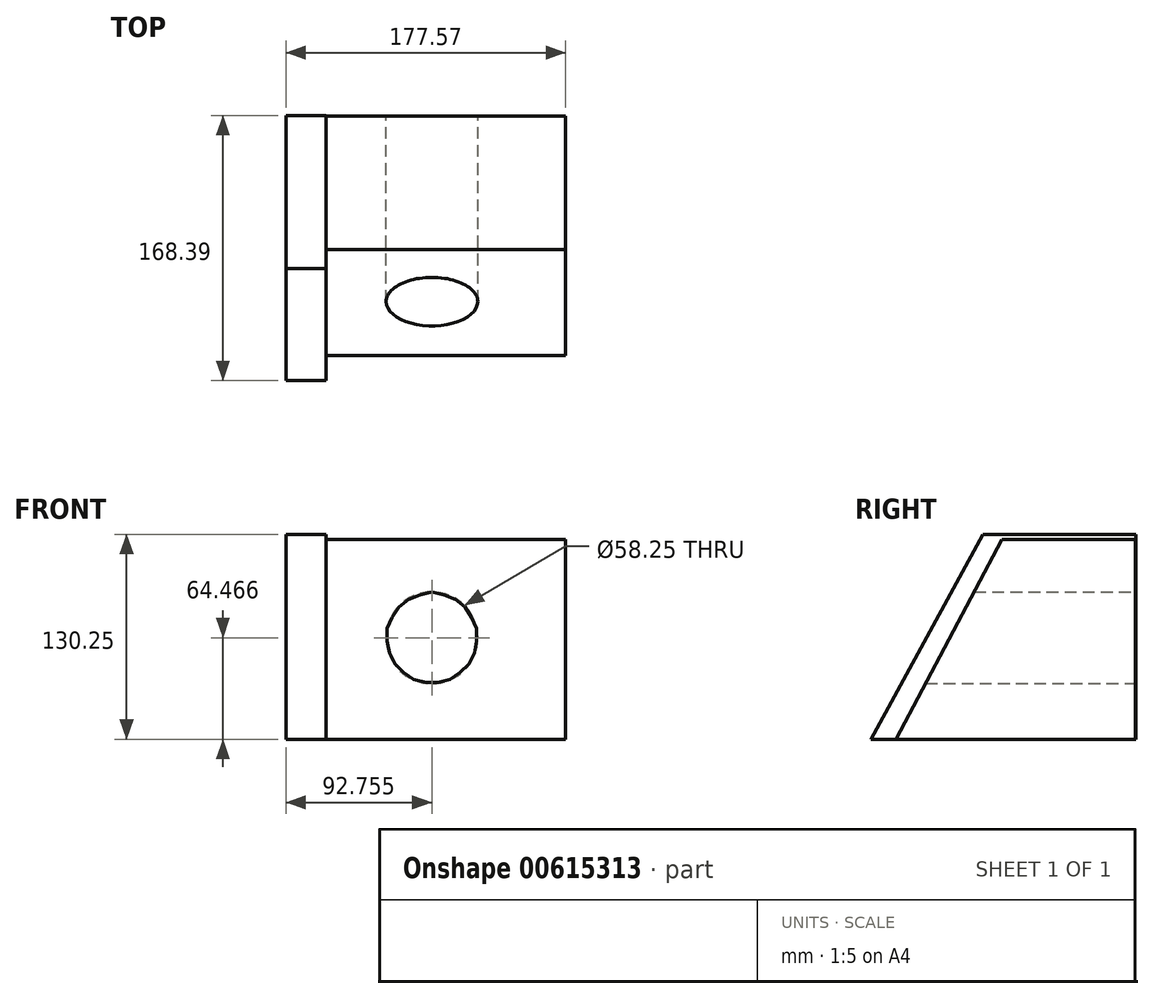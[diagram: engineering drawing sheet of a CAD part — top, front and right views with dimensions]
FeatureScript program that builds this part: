
annotation { "Feature Type Name" : "Feature", "Feature Type Description" : "" }
export const myFeature = defineFeature(function(context is Context, id is Id, definition is map)
    precondition{}
    {
        {
            var Q0;
            Q0=qCreatedBy(makeId("Top.planeOp"),FACE);
            var sketch = newSketch(context, id + "F0", { "sketchPlane" : qUnion([Q0])});
            skLineSegment(sketch, "E0.bottom", {"start": v(-75.96, -75.99) * mm, "end": v(76.2, -75.99) * mm});
            skLineSegment(sketch, "E0.top", {"start": v(-75.96, 76.13) * mm, "end": v(76.2, 76.13) * mm});
            skLineSegment(sketch, "E0.left", {"start": v(-75.96, -75.99) * mm, "end": v(-75.96, 76.13) * mm});
            skLineSegment(sketch, "E0.right", {"start": v(76.2, -75.99) * mm, "end": v(76.2, 76.13) * mm});
            skSolve(sketch);
        }
        {
            var Q0;
            Q0=makeQuery(id+"F0.imprint","IMPRINT",FACE,{"disambiguationData":[TD([[makeQuery(id+"F0.imprint","IMPRINT",EDGE,{"derivedFrom":sQuery(id+"F0.wireOp",EDGE,"E0.bottom")}),1.0]])]});
            extrude(context, id + "F1", {"entities" : qUnion([Q0]), "depth" : 127 * mm, "offsetDistance" : 25.4 * mm});
        }
        {
            var Q0;
            Q0=makeQuery(id+"F1.opExtrude","SWEPT_FACE",FACE,{"disambiguationData":[OSD([sQuery(id+"F0.wireOp",EDGE,"E0.left")])]});
            var sketch = newSketch(context, id + "F2", { "sketchPlane" : qUnion([Q0])});
            skLineSegment(sketch, "E1", {"start": v(8.65, 127) * mm, "end": v(75.99, 0) * mm});
            skLineSegment(sketch, "E2", {"start": v(75.99, 0) * mm, "end": v(75.99, 127) * mm});
            skLineSegment(sketch, "E3", {"start": v(75.99, 127) * mm, "end": v(8.65, 127) * mm});
            skSolve(sketch);
        }
        {
            var Q0;
            Q0 = qSketchRegion(id + "F2", true);
            extrude(context, id + "F3", {"entities" : qUnion([Q0]), "operationType" : NewBodyOperationType.REMOVE, "oppositeDirection" : true, "depth" : 254 * mm, "offsetDistance" : 25.4 * mm});
        }
        {
            var Q0;
            Q0=makeQuery(id+"F1.opExtrude","SWEPT_FACE",FACE,{"disambiguationData":[OSD([sQuery(id+"F0.wireOp",EDGE,"E0.top")])]});
            var sketch = newSketch(context, id + "F4", { "sketchPlane" : qUnion([Q0])});
            skCircle(sketch, "E4", {"center": v(8.6, 64.47) * mm, "radius": 29.13 * mm});
            skSolve(sketch);
        }
        {
            var Q0;
            Q0 = qSketchRegion(id + "F4", true);
            extrude(context, id + "F5", {"entities" : qUnion([Q0]), "operationType" : NewBodyOperationType.REMOVE, "oppositeDirection" : true, "depth" : 2540 * mm, "offsetDistance" : 25.4 * mm});
        }
        {
            var Q0;
            Q0=makeQuery(id+"F1.opExtrude","SWEPT_FACE",FACE,{"disambiguationData":[OSD([sQuery(id+"F0.wireOp",EDGE,"E0.left")])]});
            var sketch = newSketch(context, id + "F6", { "sketchPlane" : qUnion([Q0])});
            skLineSegment(sketch, "E5", {"start": v(-76.13, 127) * mm, "end": v(-76.13, 0) * mm});
            skLineSegment(sketch, "E6", {"start": v(-76.13, 0) * mm, "end": v(75.99, 0) * mm});
            skLineSegment(sketch, "E7", {"start": v(75.99, 0) * mm, "end": v(8.65, 127) * mm});
            skLineSegment(sketch, "E8", {"start": v(8.65, 127) * mm, "end": v(-76.13, 127) * mm});
            skSolve(sketch);
        }
        {
            var Q0;
            Q0=makeQuery(id+"F6.imprint","IMPRINT",FACE,{"disambiguationData":[TD([[makeQuery(id+"F6.imprint","IMPRINT",EDGE,{"derivedFrom":sQuery(id+"F6.wireOp",EDGE,"E5")}),1.0]])]});
            var sketch = newSketch(context, id + "F7", { "sketchPlane" : qUnion([Q0])});
            skLineSegment(sketch, "E9.bottom", {"start": v(-76.37, 130.25) * mm, "end": v(92.02, 130.25) * mm});
            skLineSegment(sketch, "E9.top", {"start": v(-76.37, 0) * mm, "end": v(92.02, 0) * mm});
            skLineSegment(sketch, "E9.left", {"start": v(-76.37, 130.25) * mm, "end": v(-76.37, 0) * mm});
            skLineSegment(sketch, "E9.right", {"start": v(92.02, 130.25) * mm, "end": v(92.02, 0) * mm});
            skSolve(sketch);
        }
        {
            var Q0;
            Q0 = qSketchRegion(id + "F7", true);
            extrude(context, id + "F8", {"entities" : qUnion([Q0]), "operationType" : NewBodyOperationType.ADD, "depth" : 25.4 * mm, "offsetDistance" : 25.4 * mm});
        }
        {
            var Q0;
            Q0=makeQuery(id+"F8.opExtrude","CAP_FACE",FACE,{"disambiguationData":[OSD([sQuery(id+"F7.wireOp",EDGE,"E9.bottom"),sQuery(id+"F7.wireOp",EDGE,"E9.top"),sQuery(id+"F7.wireOp",EDGE,"E9.left"),sQuery(id+"F7.wireOp",EDGE,"E9.right")])],"isStart":true});
            var sketch = newSketch(context, id + "F9", { "sketchPlane" : qUnion([Q0])});
            skLineSegment(sketch, "E10", {"start": v(-20.9, 130.25) * mm, "end": v(-92.02, 130.25) * mm});
            skLineSegment(sketch, "E11", {"start": v(-92.02, 130.25) * mm, "end": v(-92.02, 0) * mm});
            skLineSegment(sketch, "E12", {"start": v(-92.02, 0) * mm, "end": v(-20.9, 130.25) * mm});
            skSolve(sketch);
        }
        {
            var Q0;
            Q0 = qSketchRegion(id + "F9", true);
            extrude(context, id + "F10", {"entities" : qUnion([Q0]), "operationType" : NewBodyOperationType.REMOVE, "oppositeDirection" : true, "depth" : 2540 * mm, "offsetDistance" : 25.4 * mm});
        }
    });
